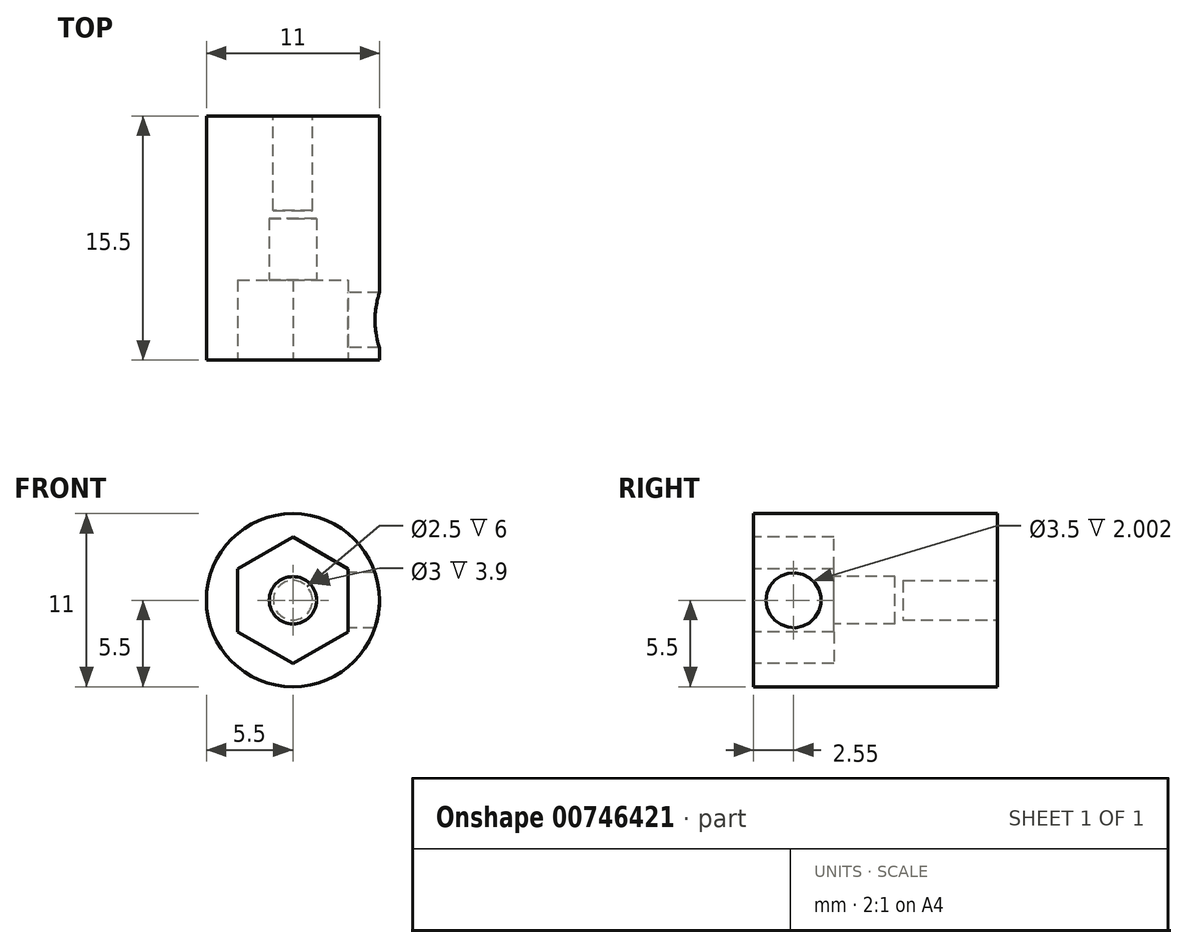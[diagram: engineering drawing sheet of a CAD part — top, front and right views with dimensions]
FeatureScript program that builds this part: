
annotation { "Feature Type Name" : "Feature", "Feature Type Description" : "" }
export const myFeature = defineFeature(function(context is Context, id is Id, definition is map)
    precondition{}
    {
        {
            var Q0;
            Q0=qCreatedBy(makeId("Top.planeOp"),FACE);
            var sketch = newSketch(context, id + "F0", { "sketchPlane" : qUnion([Q0])});
            skCircle(sketch, "E0", {"center": v(0, 0) * mm, "radius": 5.5 * mm});
            skSolve(sketch);
        }
        {
            var Q0;
            Q0=makeQuery(id+"F0.imprint","IMPRINT",FACE,{"disambiguationData":[TD([[makeQuery(id+"F0.imprint","IMPRINT",EDGE,{"derivedFrom":sQuery(id+"F0.wireOp",EDGE,"E0")}),1.0]])]});
            extrude(context, id + "F1", {"entities" : qUnion([Q0]), "depth" : 15.5 * mm, "offsetDistance" : 25.4 * mm});
        }
        {
            var Q0;
            Q0=makeQuery(id+"F1.opExtrude","CAP_FACE",FACE,{"disambiguationData":[OSD([sQuery(id+"F0.wireOp",EDGE,"E0")])],"isStart":true});
            var sketch = newSketch(context, id + "F2", { "sketchPlane" : qUnion([Q0])});
            skCircle(sketch, "E1", {"center": v(0, 0) * mm, "radius": 1.5 * mm});
            skSolve(sketch);
        }
        {
            var Q0;
            Q0 = qSketchRegion(id + "F2", true);
            extrude(context, id + "F3", {"entities" : qUnion([Q0]), "operationType" : NewBodyOperationType.REMOVE, "oppositeDirection" : true, "depth" : 9 * mm, "offsetDistance" : 25.4 * mm});
        }
        {
            var Q0;
            Q0=makeQuery(id+"F1.opExtrude","CAP_FACE",FACE,{"disambiguationData":[OSD([sQuery(id+"F0.wireOp",EDGE,"E0")])],"isStart":true});
            var sketch = newSketch(context, id + "F4", { "sketchPlane" : qUnion([Q0])});
            skPoint(sketch, "E2.middle", {"position": v(0, 0) * mm});
            skLineSegment(sketch, "E3.bottom", {"start": v(-2, 3.5) * mm, "end": v(2, 3.5) * mm});
            skLineSegment(sketch, "E3.top", {"start": v(-2, -3.5) * mm, "end": v(2, -3.5) * mm});
            skPoint(sketch, "E4", {"position": v(0, 3.5) * mm});
            skLineSegment(sketch, "E5", {"start": v(-2, 3.5) * mm, "end": v(-4.02, 0) * mm});
            skLineSegment(sketch, "E6", {"start": v(-4.02, 0) * mm, "end": v(-2, -3.5) * mm});
            skLineSegment(sketch, "E7", {"start": v(2, -3.5) * mm, "end": v(4.02, 0) * mm});
            skLineSegment(sketch, "E8", {"start": v(4.02, 0) * mm, "end": v(2, 3.5) * mm});
            skSolve(sketch);
        }
        {
            var Q0;
            Q0=makeQuery(id+"F1.opExtrude","CAP_FACE",FACE,{"disambiguationData":[OSD([sQuery(id+"F0.wireOp",EDGE,"E0")])],"isStart":false});
            var sketch = newSketch(context, id + "F5", { "sketchPlane" : qUnion([Q0])});
            skCircle(sketch, "E9", {"center": v(0, 0) * mm, "radius": 1.25 * mm});
            skSolve(sketch);
        }
        {
            var Q0;
            Q0 = qSketchRegion(id + "F5", true);
            extrude(context, id + "F6", {"entities" : qUnion([Q0]), "operationType" : NewBodyOperationType.REMOVE, "oppositeDirection" : true, "depth" : 6 * mm, "offsetDistance" : 25.4 * mm});
        }
        {
            var Q0;
            {var subQ6=sQuery(id+"F4.wireOp",EDGE,"Iv1HZIp4-Jd0e-eNyZ-4DDY-zz9OlLTtmhKp");Q0=makeQuery(id+"F4.imprint","IMPRINT",FACE,{"disambiguationData":[TD([[makeQuery(id+"F4.imprint","IMPRINT",EDGE,{"derivedFrom":subQ6}),1.0]])]});}
            var Q1;
            {var subQ5=sQuery(id+"F4.wireOp",EDGE,"H2pfqvN7-V8mH-CBbu-Zf2n-scfbZmQ49ekI");Q1=makeQuery(id+"F4.imprint","IMPRINT",FACE,{"disambiguationData":[TD([[makeQuery(id+"F4.imprint","IMPRINT",EDGE,{"derivedFrom":subQ5}),-1.0]])]});}
            var Q2;
            Q2=makeQuery(id+"F4.imprint","IMPRINT",FACE,{"disambiguationData":[TD([[makeQuery(id+"F4.imprint","IMPRINT",EDGE,{"derivedFrom":sQuery(id+"F4.wireOp",EDGE,"E3.top")}),1.0]])]});
            extrude(context, id + "F7", {"entities" : qUnion([Q0, Q1, Q2]), "operationType" : NewBodyOperationType.REMOVE, "oppositeDirection" : true, "depth" : 5.1 * mm, "offsetDistance" : 25.4 * mm});
        }
        {
            var Q0;
            Q0=makeQuery(id+"F7.boolean.opBoolean","COPY",FACE,{"derivedFrom":makeQuery(id+"F7.opExtrude","SWEPT_FACE",FACE,{"disambiguationData":[OSD([sQuery(id+"F4.wireOp",EDGE,"E3.top")])]})});
            var sketch = newSketch(context, id + "F8", { "sketchPlane" : qUnion([Q0])});
            skPoint(sketch, "E10", {"position": v(0, 0) * mm});
            skLineSegment(sketch, "E11", {"start": v(0, 0) * mm, "end": v(0, 2.55) * mm});
            skCircle(sketch, "E12", {"center": v(0, 2.55) * mm, "radius": 1.75 * mm});
            skSolve(sketch);
        }
        {
            var Q0;
            Q0=makeQuery(id+"F8.imprint","IMPRINT",FACE,{"disambiguationData":[TD([[makeQuery(id+"F8.imprint","IMPRINT",EDGE,{"derivedFrom":sQuery(id+"F8.wireOp",EDGE,"E12")}),1.0]])]});
            extrude(context, id + "F9", {"entities" : qUnion([Q0]), "operationType" : NewBodyOperationType.REMOVE, "oppositeDirection" : true, "depth" : 25.4 * mm, "offsetDistance" : 25.4 * mm});
        }
        {
            var Q0;
            Q0=qCreatedBy(makeId("Top.planeOp"),FACE);
            var sketch = newSketch(context, id + "F10", { "sketchPlane" : qUnion([Q0])});
            skLineSegment(sketch, "E13", {"start": v(-15.6, 0) * mm, "end": v(34.43, 0) * mm});
            skSolve(sketch);
        }
        {
            var Q0;
            Q0=makeQuery(id+"F1.opExtrude","SWEPT_BODY",BODY,{"disambiguationData":[OSD([sQuery(id+"F0.wireOp",EDGE,"E0")])]});
            var Q1;
            Q1=sQuery(id+"F10.wireOp",EDGE,"E13");
            transform(context, id + "F11", {"entities" : qUnion([Q0]), "transformType" : TransformType.ROTATION, "transformAxis" : qUnion([Q1]), "angle" : 180 * degree, "makeCopy" : false});
        }
        {
            var Q0;
            Q0=qCreatedBy(makeId("Top.planeOp"),FACE);
            var sketch = newSketch(context, id + "F12", { "sketchPlane" : qUnion([Q0])});
            skLineSegment(sketch, "E14", {"start": v(28.07, 0) * mm, "end": v(-32.82, 0) * mm});
            skSolve(sketch);
        }
        {
            var Q0;
            Q0=makeQuery(id+"F1.opExtrude","SWEPT_BODY",BODY,{"disambiguationData":[OSD([sQuery(id+"F0.wireOp",EDGE,"E0")])]});
            var Q1;
            Q1=sQuery(id+"F12.wireOp",EDGE,"E14");
            transform(context, id + "F13", {"entities" : qUnion([Q0]), "transformType" : TransformType.ROTATION, "transformAxis" : qUnion([Q1]), "angle" : 90 * degree, "oppositeDirection" : true, "makeCopy" : false});
        }
        {
            var Q0;
            Q0=qCreatedBy(makeId("Top.planeOp"),FACE);
            var sketch = newSketch(context, id + "F14", { "sketchPlane" : qUnion([Q0])});
            skLineSegment(sketch, "E15", {"start": v(0, 37.55) * mm, "end": v(0, -25.56) * mm});
            skSolve(sketch);
        }
        {
            var Q0;
            Q0=makeQuery(id+"F1.opExtrude","SWEPT_BODY",BODY,{"disambiguationData":[OSD([sQuery(id+"F0.wireOp",EDGE,"E0")])]});
            var Q1;
            Q1=sQuery(id+"F14.wireOp",EDGE,"E15");
            transform(context, id + "F15", {"entities" : qUnion([Q0]), "transformType" : TransformType.ROTATION, "transformAxis" : qUnion([Q1]), "angle" : 90 * degree, "makeCopy" : false});
        }
    });
